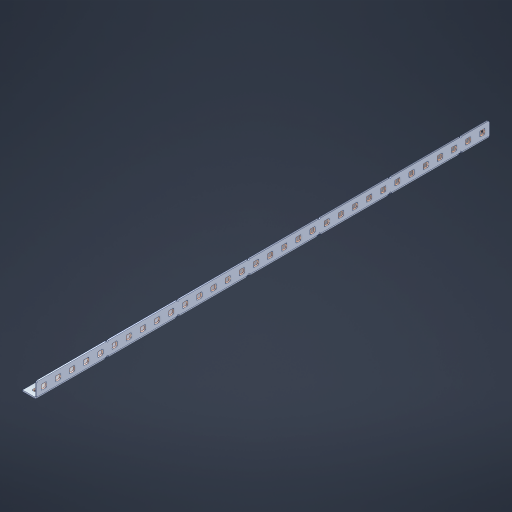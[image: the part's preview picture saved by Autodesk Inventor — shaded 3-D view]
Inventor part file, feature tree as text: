
AUTODESK INVENTOR PART (.ipt)
format: ipt  version: 2023 (Build 270158000, 158)  size: 986,624 bytes
history: native  units: in
note: dims shown in document units (in); Inventor stores cm internally (conversion verified against a paired STEP export)
features: other x69, extrude x63, sheet_metal_op x10, sketch x8, mirror x1, pattern_linear x1, chamfer x1
ambient origin geometry x8: Origin, YZ Plane, XZ Plane, XY Plane, X Axis, Y Axis, Z Axis, Center Point
bodies: Solid1 (feature_tree), Body (feature_tree)
feature tree (153):
  other  "Flange Pattern Plane"
  sheet_metal_op  "Flange Pattern"
  sheet_metal_op  "Body Pattern"
  other  "Arc Length"
  mirror  "Notch Mirror"
  pattern_linear  "Notch Pattern"  Spacing1=0.1875in  [1 undecoded]
  chamfer  "End Chamfer"
  extrude  "Half Cut"  Depth=0.0469in
  sketch  "Sketch1"  dims[d0=2.5in]
  other  "Plate1"
  sketch  "Sketch2"  dims[d1=16.0in]
  other  "Plate2"
  sheet_metal_op  "Bend1"
  sheet_metal_op  "Corner1"
  sketch  "Sketch3"  dims[d2=0.0469in]
  other  "Flange Pattern Sketch"
  sketch  "Sketch7"  dims[d3=0.0469in]
  other  "Srf1"
  other  "Srf2"
  sketch  "Sketch8"  dims[d4=0.0234in]
  sketch  "Sketch9"  dims[d5=0.0938in]
  other  "Srf91"
  sheet_metal_op  "Body Pattern Sketch"
  other  "Srf92"
  sketch  "Sketch13"  dims[d6=0.0469in]
  sketch  "Sketch14"  dims[d7=0.5in d8=90.0deg d9=0.0312in d10=0.1875in d11=0.0469in d12=0.0469in d16=0.182in d17=0.02in d18=0.0469in d19=0.0in d20=0.25in d21=0.25in d46=0.172in d47=1.0in d48=0.0in d49=0.182in d50=0.02in d51=0.25in d52=0.25in d53=0.0469in d54=0.0in d55=0.172in d56=1.0in d57=0.0in d60=12.5984in d62=0.5in d63=0.3937in d65=0.5in d85=0.1227in d86=0.1659in d88=0.04in d89=0.0469in d90=0.0in d91=0.04in d92=0.0491in d95=2.5in d96=0.04in d97=0.25in d98=45.0deg d101=0.0in d102=2.497in d131=0.5in d132=12.5984in d134=0.5in d139=0.5in]
  other  "Srf856"
  other  "Srf1310"
  other  "Srf1311"
  other  "Srf1312"
  other  "Srf1376"
  other  "Srf1377"
  other  "Srf1728"
  other  "Srf1755"
  other  "Srf1878"
  other  "Srf1879"
  other  "Srf1880"
  other  "Srf1881"
  other  "Srf1882"
  other  "Srf1883"
  other  "Srf1884"
  other  "Srf1885"
  other  "Srf1886"
  other  "Srf1887"
  other  "Srf1888"
  other  "Srf1889"
  other  "Srf1890"
  other  "Srf1891"
  other  "Srf1892"
  other  "Srf1893"
  other  "Srf1894"
  other  "Srf1895"
  other  "Srf1896"
  other  "Srf1897"
  other  "Srf1898"
  other  "Srf1899"
  other  "Srf1900"
  other  "Srf1901"
  other  "Srf1902"
  other  "Srf1903"
  other  "Srf1942"
  other  "Srf1943"
  other  "Srf1944"
  other  "Srf1945"
  other  "Srf1946"
  other  "Srf1947"
  other  "Srf1948"
  other  "Srf1949"
  other  "Srf1950"
  other  "Srf1951"
  other  "Srf1952"
  other  "Srf1953"
  other  "Srf1954"
  other  "Srf1955"
  other  "Srf1956"
  other  "Srf1957"
  other  "Srf1958"
  other  "Srf1959"
  other  "Srf1960"
  other  "Srf1961"
  other  "Srf1962"
  other  "Srf1963"
  other  "Srf1964"
  other  "Srf1965"
  other  "Srf1966"
  other  "Srf1967"
  sheet_metal_op  "Flange Stamp"
  sheet_metal_op  "Flange Circle"
  sheet_metal_op  "Body Stamp"
  sheet_metal_op  "Body Circle"
  sheet_metal_op  "Notch"
  extrude  "ExtrusionSrf2"  Depth=0.0469in
  extrude  "ExtrusionSrf92"  Depth=0.5in
  extrude  "ExtrusionSrf856"  Depth=0.02in
  extrude  "ExtrusionSrf1310"  Depth=0.0469in
  extrude  "ExtrusionSrf1311"  TaperAngle=0.0deg  [1 undecoded]
  extrude  "ExtrusionSrf1312"  Depth=0.5in
  extrude  "ExtrusionSrf1376"  Depth=0.5in
  extrude  "ExtrusionSrf1377"  Depth=0.5in
  extrude  "ExtrusionSrf1728"  Depth=0.5in TaperAngle=0.0deg
  extrude  "ExtrusionSrf1755"  Depth=0.5in
  extrude  "ExtrusionSrf1878"  Depth=0.02in
  extrude  "ExtrusionSrf1879"  Depth=0.5in
  extrude  "ExtrusionSrf1880"  Depth=0.5in
  extrude  "ExtrusionSrf1881"  Depth=0.0469in
  extrude  "ExtrusionSrf1882"  TaperAngle=0.0deg  [1 undecoded]
  extrude  "ExtrusionSrf1883"  Depth=0.5in
  extrude  "ExtrusionSrf1884"  Depth=0.5in TaperAngle=0.0deg
  extrude  "ExtrusionSrf1885"  Depth=0.5in
  extrude  "ExtrusionSrf1886"  Depth=0.5in
  extrude  "ExtrusionSrf1887"  Depth=0.5in
  extrude  "ExtrusionSrf1888"  Depth=0.5in
  extrude  "ExtrusionSrf1889"  Depth=0.5in
  extrude  "ExtrusionSrf1890"  Depth=0.0469in
  extrude  "ExtrusionSrf1891"  TaperAngle=0.0deg  [1 undecoded]
  extrude  "ExtrusionSrf1892"  Depth=0.5in
  extrude  "ExtrusionSrf1893"  Depth=0.5in
  extrude  "ExtrusionSrf1894"  Depth=0.5in
  extrude  "ExtrusionSrf1895"  Depth=0.5in TaperAngle=45.0deg
  extrude  "ExtrusionSrf1896"  TaperAngle=0.0deg  [1 undecoded]
  extrude  "ExtrusionSrf1897"  Depth=0.5in
  extrude  "ExtrusionSrf1898"  Depth=0.5in
  extrude  "ExtrusionSrf1899"  Depth=0.5in
  extrude  "ExtrusionSrf1900"  Depth=0.5in
  extrude  "ExtrusionSrf1901"  Depth=0.5in
  extrude  "ExtrusionSrf1902"  [1 undecoded]
  extrude  "ExtrusionSrf1903"  [1 undecoded]
  extrude  "ExtrusionSrf1942"  [1 undecoded]
  extrude  "ExtrusionSrf1943"  [1 undecoded]
  extrude  "ExtrusionSrf1944"  [1 undecoded]
  extrude  "ExtrusionSrf1945"  [1 undecoded]
  extrude  "ExtrusionSrf1946"  [1 undecoded]
  extrude  "ExtrusionSrf1947"  [1 undecoded]
  extrude  "ExtrusionSrf1948"  [1 undecoded]
  extrude  "ExtrusionSrf1949"  [1 undecoded]
  extrude  "ExtrusionSrf1950"  [1 undecoded]
  extrude  "ExtrusionSrf1951"  [1 undecoded]
  extrude  "ExtrusionSrf1952"  [1 undecoded]
  extrude  "ExtrusionSrf1953"  [1 undecoded]
  extrude  "ExtrusionSrf1954"  [1 undecoded]
  extrude  "ExtrusionSrf1955"  [1 undecoded]
  extrude  "ExtrusionSrf1956"  [1 undecoded]
  extrude  "ExtrusionSrf1957"  [1 undecoded]
  extrude  "ExtrusionSrf1958"  [1 undecoded]
  extrude  "ExtrusionSrf1959"  [1 undecoded]
  extrude  "ExtrusionSrf1960"  [1 undecoded]
  extrude  "ExtrusionSrf1961"  [1 undecoded]
  extrude  "ExtrusionSrf1962"  [1 undecoded]
  extrude  "ExtrusionSrf1963"  [1 undecoded]
  extrude  "ExtrusionSrf1964"  [1 undecoded]
  extrude  "ExtrusionSrf1965"  [1 undecoded]
  extrude  "ExtrusionSrf1966"  [1 undecoded]
  extrude  "ExtrusionSrf1967"  [1 undecoded]
note: 33 required parameter values undecoded (feature->parameter linkage not recoverable at this tier; creation-order binding heuristic only, values carry confidence <= 0.55)
